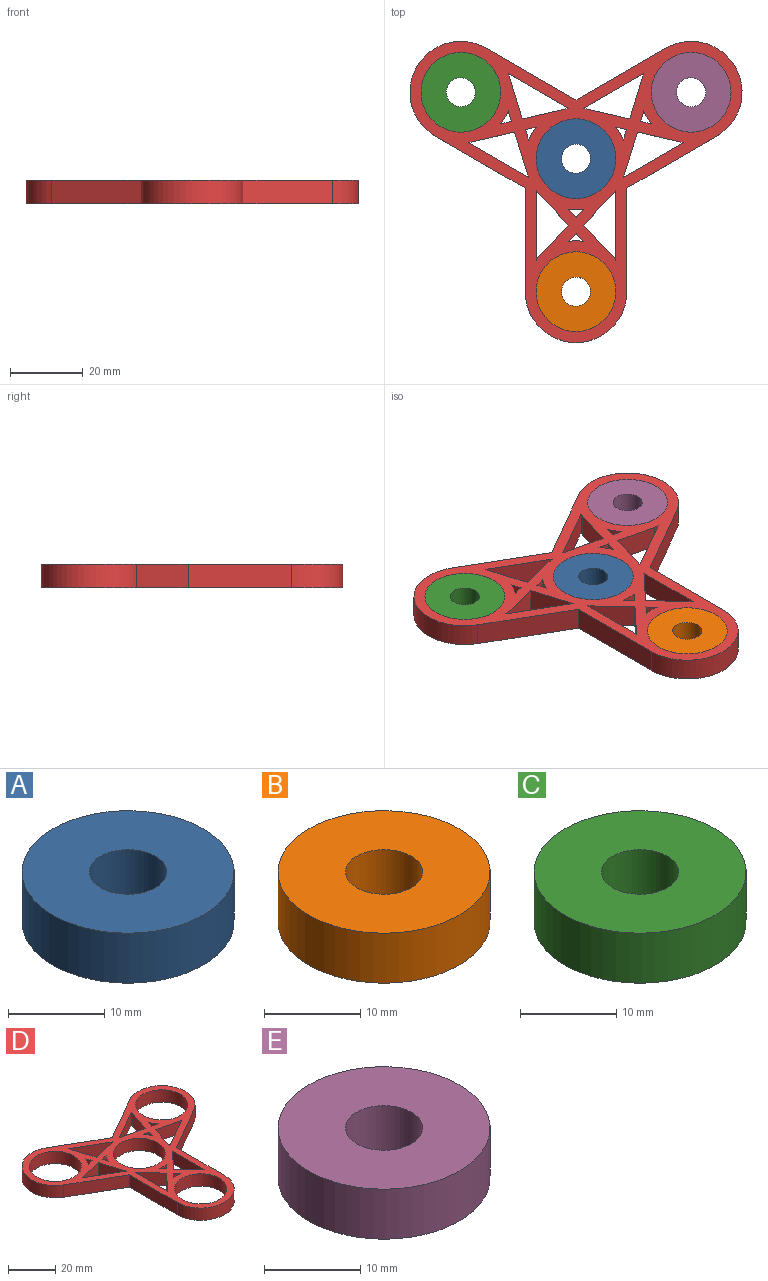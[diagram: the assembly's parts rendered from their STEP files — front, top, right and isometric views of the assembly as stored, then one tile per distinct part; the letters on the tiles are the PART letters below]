
ASSEMBLY  parts=5 mates=4
PART A: 4 faces, bbox 22x22x6.4 mm
  f0: cylinder r=4mm len=8mm, axis (0,0,-1), area 159.6mm2, adj f2,f3
  f1: cylinder r=11mm len=22mm, axis (0,0,-1), area 438.9mm2, adj f2,f3
  f2: plane 22x22mm, normal (0,0,1), area 329.9mm2, adj f0,f1
  f3: plane 22x22mm, normal (0,0,-1), area 329.9mm2, adj f0,f1
PART B: 4 faces, bbox 22x22x6.4 mm
  f0: cylinder r=4mm len=8mm, axis (0,0,-1), area 159.6mm2, adj f2,f3
  f1: cylinder r=11mm len=22mm, axis (0,0,-1), area 438.9mm2, adj f2,f3
  f2: plane 22x22mm, normal (0,0,1), area 329.9mm2, adj f0,f1
  f3: plane 22x22mm, normal (0,0,-1), area 329.9mm2, adj f0,f1
PART C: 4 faces, bbox 22x22x6.4 mm
  f0: cylinder r=4mm len=8mm, axis (0,0,-1), area 159.6mm2, adj f2,f3
  f1: cylinder r=11mm len=22mm, axis (0,0,-1), area 438.9mm2, adj f2,f3
  f2: plane 22x22mm, normal (0,0,1), area 329.9mm2, adj f0,f1
  f3: plane 22x22mm, normal (0,0,-1), area 329.9mm2, adj f0,f1
PART D: 63 faces, bbox 91.6x83.1x6.4 mm
  f0: plane 6.35x2.92mm, normal (0.96,0.29,0), area 19.4mm2, adj f1,f60,f61,f62
  f1: plane 6.35x2.98mm, normal (0.23,-0.97,0), area 19.4mm2, adj f0,f60,f61,f62
  f2: plane 11.66x6.35mm, normal (0.23,-0.97,0), area 76mm2, adj f3,f44,f61,f62
  f3: plane 11.46x6.35mm, normal (-0.96,-0.29,0), area 76mm2, adj f2,f4,f61,f62
  f4: cylinder r=14.03mm len=6.35mm, axis (0,0,-1), area 7.3mm2, adj f3,f5,f61,f62
  f5: plane 16.66x9.62mm, normal (0.5,0.87,0), area 122.1mm2, adj f4,f44,f61,f62
  f6: plane 6.35x2.98mm, normal (-0.23,0.97,0), area 19.4mm2, adj f7,f45,f61,f62
  f7: cylinder r=14.03mm len=6.35mm, axis (0,0,-1), area 26.6mm2, adj f6,f45,f61,f62
  f8: plane 11.46x6.35mm, normal (0.96,0.29,0), area 76mm2, adj f9,f46,f61,f62
  f9: cylinder r=14.03mm len=6.35mm, axis (0,0,-1), area 7.3mm2, adj f8,f10,f61,f62
  f10: plane 16.66x9.62mm, normal (-0.5,-0.87,0), area 122.1mm2, adj f9,f11,f61,f62
  f11: cylinder r=14.03mm len=6.35mm, axis (0,0,-1), area 7.3mm2, adj f10,f46,f61,f62
  f12: plane 6.35x2.92mm, normal (0.96,-0.29,0), area 19.4mm2, adj f13,f47,f61,f62
  f13: cylinder r=14.03mm len=6.35mm, axis (0,0,-1), area 26.6mm2, adj f12,f47,f61,f62
  f14: plane 16.66x9.62mm, normal (-0.5,0.87,0), area 122.1mm2, adj f15,f48,f61,f62
  f15: cylinder r=14.03mm len=6.35mm, axis (0,0,-1), area 7.3mm2, adj f14,f16,f61,f62
  f16: plane 11.46x6.35mm, normal (0.96,-0.29,0), area 76mm2, adj f15,f17,f61,f62
  f17: plane 11.66x6.35mm, normal (-0.23,-0.97,0), area 76mm2, adj f16,f48,f61,f62
  f18: plane 11.66x6.35mm, normal (0.23,0.97,0), area 76mm2, adj f19,f49,f61,f62
  f19: cylinder r=14.03mm len=6.35mm, axis (0,0,-1), area 7.3mm2, adj f18,f20,f61,f62
  f20: plane 16.66x9.62mm, normal (0.5,-0.87,0), area 122.1mm2, adj f19,f21,f61,f62
  f21: cylinder r=14.03mm len=6.35mm, axis (0,0,-1), area 7.3mm2, adj f20,f49,f61,f62
  f22: plane 6.35x2.23mm, normal (0.73,0.68,0), area 19.4mm2, adj f23,f50,f61,f62
  f23: cylinder r=14.03mm len=6.35mm, axis (0,0,-1), area 26.6mm2, adj f22,f50,f61,f62
  f24: cylinder r=14.03mm len=6.35mm, axis (0,0,-1), area 26.6mm2, adj f25,f51,f61,f62
  f25: plane 6.35x2.23mm, normal (0.73,-0.68,0), area 19.4mm2, adj f24,f51,f61,f62
  f26: plane 8.75x8.18mm, normal (0.73,-0.68,0), area 76mm2, adj f27,f52,f61,f62
  f27: cylinder r=14.03mm len=6.35mm, axis (0,0,-1), area 7.3mm2, adj f26,f28,f61,f62
  f28: plane 19.23x6.35mm, normal (-1,0,0), area 122.1mm2, adj f27,f29,f61,f62
  f29: cylinder r=14.03mm len=6.35mm, axis (0,0,-1), area 7.3mm2, adj f28,f52,f61,f62
  f30: plane 24.73x14.28mm, normal (-0.5,0.87,0), area 181.4mm2, adj f31,f53,f61,f62
  f31: plane 24.73x14.28mm, normal (0.5,0.87,0), area 181.4mm2, adj f30,f32,f61,f62
  f32: cylinder r=14.03mm len=26.19mm, axis (0,0,-1), area 280mm2, adj f31,f33,f61,f62
  f33: plane 24.73x14.28mm, normal (-0.5,-0.87,0), area 181.4mm2, adj f32,f34,f61,f62
  f34: plane 28.56x6.35mm, normal (-1,0,0), area 181.4mm2, adj f33,f35,f61,f62
  f35: cylinder r=14.03mm len=28.07mm, axis (0,0,-1), area 280mm2, adj f34,f36,f61,f62
  f36: plane 28.56x6.35mm, normal (1,0,0), area 181.4mm2, adj f35,f37,f61,f62
  f37: plane 24.73x14.28mm, normal (0.5,-0.87,0), area 181.4mm2, adj f36,f53,f61,f62
  f38: plane 19.23x6.35mm, normal (1,0,0), area 122.1mm2, adj f39,f58,f61,f62
  f39: cylinder r=14.03mm len=6.35mm, axis (0,0,-1), area 7.3mm2, adj f38,f40,f61,f62
  f40: plane 8.75x8.18mm, normal (-0.73,-0.68,0), area 76mm2, adj f39,f41,f61,f62
  f41: plane 8.75x8.18mm, normal (-0.73,0.68,0), area 76mm2, adj f40,f58,f61,f62
  f42: plane 6.35x2.92mm, normal (-0.96,0.29,0), area 19.4mm2, adj f43,f59,f61,f62
  f43: cylinder r=14.03mm len=6.35mm, axis (0,0,-1), area 26.6mm2, adj f42,f59,f61,f62
  f44: cylinder r=14.03mm len=6.35mm, axis (0,0,-1), area 7.3mm2, adj f2,f5,f61,f62
  f45: plane 6.35x2.92mm, normal (-0.96,-0.29,0), area 19.4mm2, adj f6,f7,f61,f62
  f46: plane 11.66x6.35mm, normal (-0.23,0.97,0), area 76mm2, adj f8,f11,f61,f62
  f47: plane 6.35x2.98mm, normal (0.23,0.97,0), area 19.4mm2, adj f12,f13,f61,f62
  f48: cylinder r=14.03mm len=6.35mm, axis (0,0,-1), area 7.3mm2, adj f14,f17,f61,f62
  f49: plane 11.46x6.35mm, normal (-0.96,0.29,0), area 76mm2, adj f18,f21,f61,f62
  f50: plane 6.35x2.23mm, normal (-0.73,0.68,0), area 19.4mm2, adj f22,f23,f61,f62
  f51: plane 6.35x2.23mm, normal (-0.73,-0.68,0), area 19.4mm2, adj f24,f25,f61,f62
  f52: plane 8.75x8.18mm, normal (0.73,0.68,0), area 76mm2, adj f26,f29,f61,f62
  f53: cylinder r=14.03mm len=26.19mm, axis (0,0,-1), area 280mm2, adj f30,f37,f61,f62
  f54: cylinder r=11mm len=22mm, axis (0,0,-1), area 438.9mm2, adj f61,f62
  f55: cylinder r=11mm len=22mm, axis (0,0,-1), area 438.9mm2, adj f61,f62
  f56: cylinder r=11mm len=22mm, axis (0,0,-1), area 438.9mm2, adj f61,f62
  f57: cylinder r=11mm len=22mm, axis (0,0,-1), area 438.9mm2, adj f61,f62
  f58: cylinder r=14.03mm len=6.35mm, axis (0,0,-1), area 7.3mm2, adj f38,f41,f61,f62
  f59: plane 6.35x2.98mm, normal (-0.23,-0.97,0), area 19.4mm2, adj f42,f43,f61,f62
  f60: cylinder r=14.03mm len=6.35mm, axis (0,0,-1), area 26.6mm2, adj f0,f1,f61,f62
  f61: plane 91.57x83.06mm, normal (0,0,1), area 1616.6mm2, adj f0,f1,f2,f3,f4,f5,f6,f7
  f62: plane 91.57x83.06mm, normal (0,0,-1), area 1616.6mm2, adj f0,f1,f2,f3,f4,f5,f6,f7
PART E: 4 faces, bbox 22x22x6.4 mm
  f0: cylinder r=4mm len=8mm, axis (0,0,-1), area 159.6mm2, adj f2,f3
  f1: cylinder r=11mm len=22mm, axis (0,0,-1), area 438.9mm2, adj f2,f3
  f2: plane 22x22mm, normal (0,0,1), area 329.9mm2, adj f0,f1
  f3: plane 22x22mm, normal (0,0,-1), area 329.9mm2, adj f0,f1
PLACE A t=(-25.48,-24.63,31.23)mm
PLACE B t=(-62.41,-73.29,31.23)mm
PLACE C t=(-120.16,-7.83,31.23)mm
PLACE D t=(-65.02,26.92,31.23)mm
PLACE E t=(-25.65,3.63,31.23)mm
MATE fastened B.f0 <-> D.f35  axis (0,0,-1) through (-65.02,-9.74,31.23)mm
MATE fastened D.f13 <-> E.f0  axis (0,0,-1) through (-33.27,45.25,31.23)mm
MATE fastened C.f0 <-> D.f7  axis (0,0,-1) through (-96.77,45.25,31.23)mm
MATE fastened A.f0 <-> D.f54  axis (0,0,-1) through (-65.02,26.92,31.23)mm
